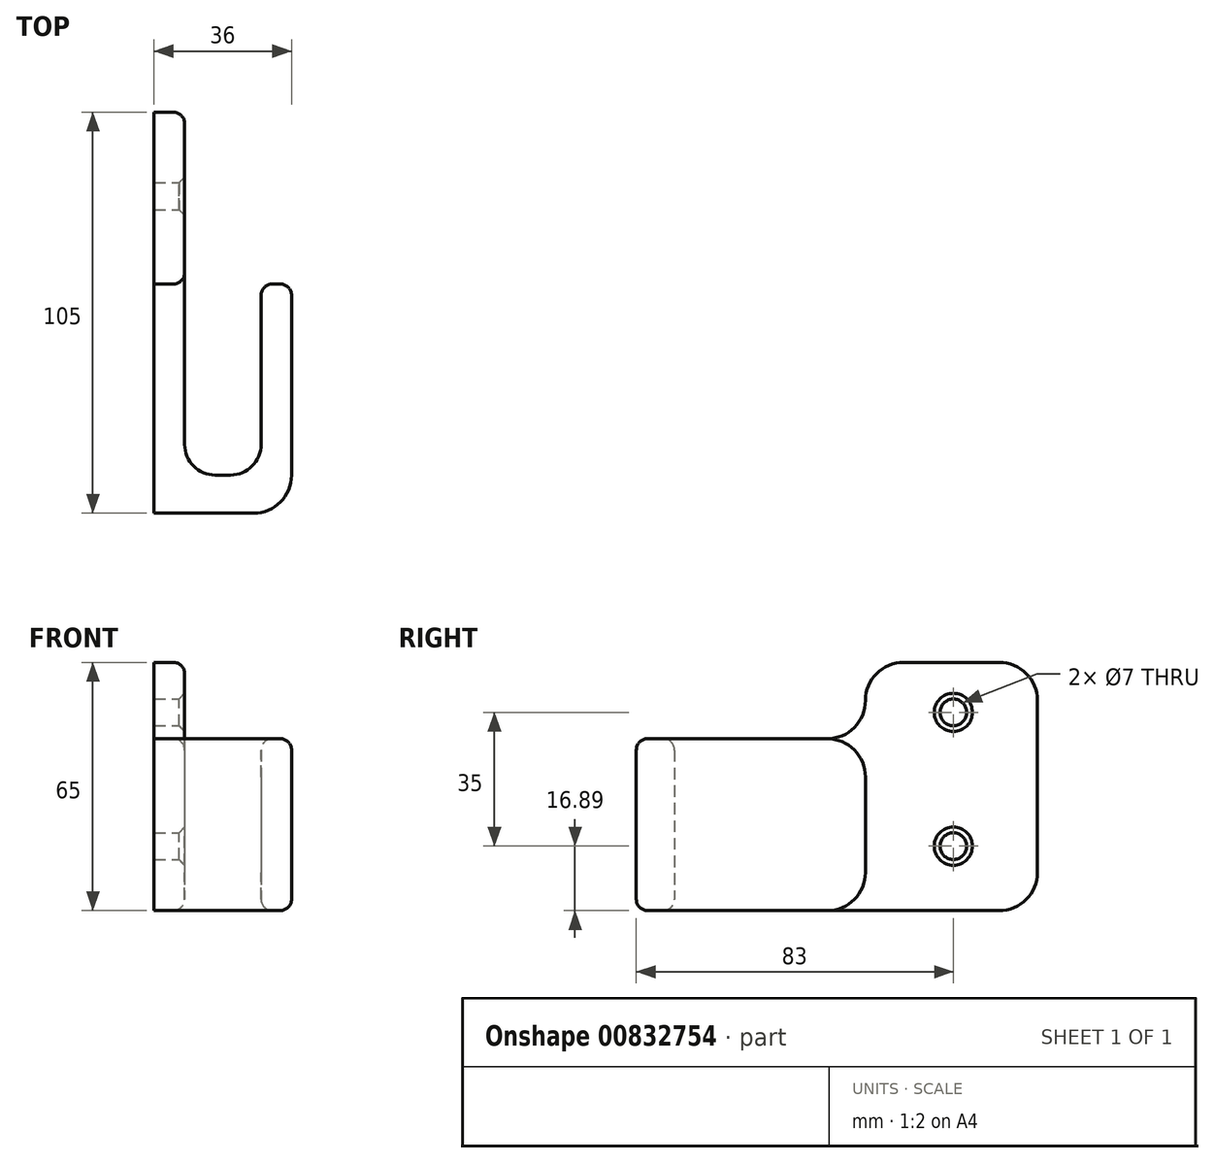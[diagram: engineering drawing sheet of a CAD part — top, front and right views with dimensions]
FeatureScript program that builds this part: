
annotation { "Feature Type Name" : "Feature", "Feature Type Description" : "" }
export const myFeature = defineFeature(function(context is Context, id is Id, definition is map)
    precondition{}
    {
        {
            var Q0;
            Q0=qCreatedBy(makeId("Top.planeOp"),FACE);
            var sketch = newSketch(context, id + "F0", { "sketchPlane" : qUnion([Q0])});
            skLineSegment(sketch, "E0.bottom", {"start": v(0, 105) * mm, "end": v(8, 105) * mm});
            skLineSegment(sketch, "E0.top", {"start": v(0, 0) * mm, "end": v(36, 0) * mm});
            skLineSegment(sketch, "E0.left", {"start": v(0, 105) * mm, "end": v(0, 0) * mm});
            skLineSegment(sketch, "E0.right", {"start": v(36, 60) * mm, "end": v(36, 0) * mm});
            skLineSegment(sketch, "E1.top", {"start": v(8, 10) * mm, "end": v(28, 10) * mm});
            skLineSegment(sketch, "E1.left", {"start": v(8, 105) * mm, "end": v(8, 10) * mm});
            skLineSegment(sketch, "E1.right", {"start": v(28, 60) * mm, "end": v(28, 10) * mm});
            skLineSegment(sketch, "E2", {"start": v(28, 60) * mm, "end": v(36, 60) * mm});
            skSolve(sketch);
        }
        {
            var Q0;
            Q0 = qSketchRegion(id + "F0", true);
            extrude(context, id + "F1", {"entities" : qUnion([Q0]), "depth" : 45 * mm, "offsetDistance" : 25 * mm});
        }
        {
            var Q0;
            Q0=qCreatedBy(makeId("Right.planeOp"),FACE);
            var sketch = newSketch(context, id + "F2", { "sketchPlane" : qUnion([Q0])});
            skLineSegment(sketch, "E3.bottom", {"start": v(105, 65) * mm, "end": v(60, 65) * mm});
            skLineSegment(sketch, "E3.top", {"start": v(105, 0) * mm, "end": v(60, 0) * mm});
            skLineSegment(sketch, "E3.left", {"start": v(105, 65) * mm, "end": v(105, 0) * mm});
            skLineSegment(sketch, "E3.right", {"start": v(60, 65) * mm, "end": v(60, 0) * mm});
            skSolve(sketch);
        }
        {
            var Q0;
            Q0 = qSketchRegion(id + "F2", true);
            var Q1;
            Q1=makeQuery(id+"F1.opExtrude","SWEPT_FACE",FACE,{"disambiguationData":[OSD([sQuery(id+"F0.wireOp",EDGE,"E1.left")])]});
            extrude(context, id + "F3", {"entities" : qUnion([Q0]), "operationType" : NewBodyOperationType.ADD, "endBound" : BoundingType.UP_TO_SURFACE, "depth" : 25 * mm, "endBoundEntityFace" : qUnion([Q1]), "offsetDistance" : 25 * mm});
        }
        {
            var Q0;
            Q0=makeQuery(id+"F3.boolean.opBoolean","INTERSECT",EDGE,{"derivedFrom":[makeQuery(id+"F1.opExtrude","CAP_FACE",FACE,{"disambiguationData":[OSD([sQuery(id+"F0.wireOp",EDGE,"E0.bottom"),sQuery(id+"F0.wireOp",EDGE,"E0.top"),sQuery(id+"F0.wireOp",EDGE,"E0.left"),sQuery(id+"F0.wireOp",EDGE,"E0.right"),sQuery(id+"F0.wireOp",EDGE,"E1.top"),sQuery(id+"F0.wireOp",EDGE,"E1.left"),sQuery(id+"F0.wireOp",EDGE,"E1.right"),sQuery(id+"F0.wireOp",EDGE,"E2")])],"isStart":false}),makeQuery(id+"F3.opExtrude","SWEPT_FACE",FACE,{"disambiguationData":[OSD([sQuery(id+"F2.wireOp",EDGE,"E3.right")])]})]});
            var Q1;
            Q1=makeQuery(id+"F3.boolean.opBoolean","INTERSECT",EDGE,{"derivedFrom":[makeQuery(id+"F1.opExtrude","CAP_FACE",FACE,{"disambiguationData":[OSD([sQuery(id+"F0.wireOp",EDGE,"E0.bottom"),sQuery(id+"F0.wireOp",EDGE,"E0.top"),sQuery(id+"F0.wireOp",EDGE,"E0.left"),sQuery(id+"F0.wireOp",EDGE,"E0.right"),sQuery(id+"F0.wireOp",EDGE,"E1.top"),sQuery(id+"F0.wireOp",EDGE,"E1.left"),sQuery(id+"F0.wireOp",EDGE,"E1.right"),sQuery(id+"F0.wireOp",EDGE,"E2")])],"isStart":true}),makeQuery(id+"F3.opExtrude","SWEPT_FACE",FACE,{"disambiguationData":[OSD([sQuery(id+"F2.wireOp",EDGE,"E3.right")])]})]});
            var Q2;
            Q2=makeQuery(id+"F3.opExtrude","SWEPT_EDGE",EDGE,{"disambiguationData":[OSD([sQuery(id+"F2.wireOp",EDGE,"E3.top"),sQuery(id+"F2.wireOp",EDGE,"E3.right")])]});
            var Q3;
            Q3=makeQuery(id+"F3.opExtrude","SWEPT_EDGE",EDGE,{"disambiguationData":[OSD([sQuery(id+"F2.wireOp",EDGE,"E3.top"),sQuery(id+"F2.wireOp",EDGE,"E3.left")])]});
            var Q4;
            Q4=makeQuery(id+"F3.opExtrude","SWEPT_EDGE",EDGE,{"disambiguationData":[OSD([sQuery(id+"F2.wireOp",EDGE,"E3.bottom"),sQuery(id+"F2.wireOp",EDGE,"E3.left")])]});
            var Q5;
            Q5=makeQuery(id+"F3.opExtrude","SWEPT_EDGE",EDGE,{"disambiguationData":[OSD([sQuery(id+"F2.wireOp",EDGE,"E3.bottom"),sQuery(id+"F2.wireOp",EDGE,"E3.right")])]});
            var Q6;
            Q6=makeQuery(id+"F1.opExtrude","CAP_EDGE",EDGE,{"disambiguationData":[OSD([sQuery(id+"F0.wireOp",EDGE,"E2")])],"isStart":false});
            var Q7;
            Q7=makeQuery(id+"F1.opExtrude","CAP_EDGE",EDGE,{"disambiguationData":[OSD([sQuery(id+"F0.wireOp",EDGE,"E2")])],"isStart":true});
            var Q8;
            Q8=makeQuery(id+"F1.opExtrude","CAP_EDGE",EDGE,{"disambiguationData":[OSD([sQuery(id+"F0.wireOp",EDGE,"E0.bottom")])],"isStart":true});
            fillet(context, id + "F4", {"entities" : qUnion([Q0, Q1, Q2, Q3, Q4, Q5, Q6, Q7, Q8]), "radius" : 10 * mm, "tangentPropagation" : true, "allowEdgeOverflow" : false});
        }
        {
            var Q0;
            Q0=makeQuery(id+"F1.opExtrude","SWEPT_EDGE",EDGE,{"disambiguationData":[OSD([sQuery(id+"F0.wireOp",EDGE,"E0.top"),sQuery(id+"F0.wireOp",EDGE,"E0.right")])]});
            fillet(context, id + "F5", {"entities" : qUnion([Q0]), "radius" : 10 * mm, "tangentPropagation" : true, "allowEdgeOverflow" : false});
        }
        {
            var Q0;
            Q0=makeQuery(id+"F1.opExtrude","SWEPT_EDGE",EDGE,{"disambiguationData":[OSD([sQuery(id+"F0.wireOp",EDGE,"E1.top"),sQuery(id+"F0.wireOp",EDGE,"E1.left")])]});
            var Q1;
            Q1=makeQuery(id+"F1.opExtrude","SWEPT_EDGE",EDGE,{"disambiguationData":[OSD([sQuery(id+"F0.wireOp",EDGE,"E1.top"),sQuery(id+"F0.wireOp",EDGE,"E1.right")])]});
            fillet(context, id + "F6", {"entities" : qUnion([Q0, Q1]), "radius" : 8 * mm, "tangentPropagation" : true, "allowEdgeOverflow" : false});
        }
        {
            var Q0;
            Q0=makeQuery(id+"F1.opExtrude","SWEPT_FACE",FACE,{"disambiguationData":[OSD([sQuery(id+"F0.wireOp",EDGE,"E0.right")])]});
            var Q1;
            {var subQ0=sQuery(id+"F0.wireOp",EDGE,"E1.left");Q1=makeQuery(id+"F3.boolean.opBoolean","MERGE",FACE,{"derivedFrom":[makeQuery(id+"F1.opExtrude","SWEPT_FACE",FACE,{"disambiguationData":[OSD([subQ0])]}),makeQuery(id+"F3.opExtrude","CAP_FACE",FACE,{"disambiguationData":[OSD([subQ0])],"isStart":false})]});}
            fillet(context, id + "F7", {"entities" : qUnion([Q0, Q1]), "radius" : 3 * mm, "tangentPropagation" : true, "allowEdgeOverflow" : false});
        }
        {
            var Q0;
            {var subQ0=sQuery(id+"F0.wireOp",EDGE,"E1.left");Q0=makeQuery(id+"F3.boolean.opBoolean","MERGE",FACE,{"derivedFrom":[makeQuery(id+"F1.opExtrude","SWEPT_FACE",FACE,{"disambiguationData":[OSD([subQ0])]}),makeQuery(id+"F3.opExtrude","CAP_FACE",FACE,{"disambiguationData":[OSD([subQ0])],"isStart":false})]});}
            var sketch = newSketch(context, id + "F8", { "sketchPlane" : qUnion([Q0])});
            skPoint(sketch, "E4", {"position": v(83, 51.89) * mm});
            skPoint(sketch, "E5", {"position": v(83, 16.89) * mm});
            skSolve(sketch);
        }
        {
            var Q0;
            Q0=sQuery(id+"F8.wireOp",VERTEX,"E4");
            var Q1;
            Q1=sQuery(id+"F8.wireOp",VERTEX,"E5");
            var Q2;
            Q2=makeQuery(id+"F1.opExtrude","SWEPT_BODY",BODY,{"disambiguationData":[OSD([sQuery(id+"F0.wireOp",EDGE,"E0.bottom"),sQuery(id+"F0.wireOp",EDGE,"E0.top"),sQuery(id+"F0.wireOp",EDGE,"E0.left"),sQuery(id+"F0.wireOp",EDGE,"E0.right"),sQuery(id+"F0.wireOp",EDGE,"E1.top"),sQuery(id+"F0.wireOp",EDGE,"E1.left"),sQuery(id+"F0.wireOp",EDGE,"E1.right"),sQuery(id+"F0.wireOp",EDGE,"E2")])]});
            hole(context, id + "F9", {"style" : HoleStyle.C_SINK, "endStyle" : HoleEndStyle.THROUGH, "holeDiameter" : 7 * mm, "cSinkDiameter" : 10 * mm, "cSinkAngle" : 90 * degree, "majorDiameter" : 5 * mm, "isTappedThrough" : true, "tappedDepth" : 12 * mm, "tapClearance" : 3, "locations" : qUnion([Q0, Q1]), "scope" : qUnion([Q2])});
        }
    });
